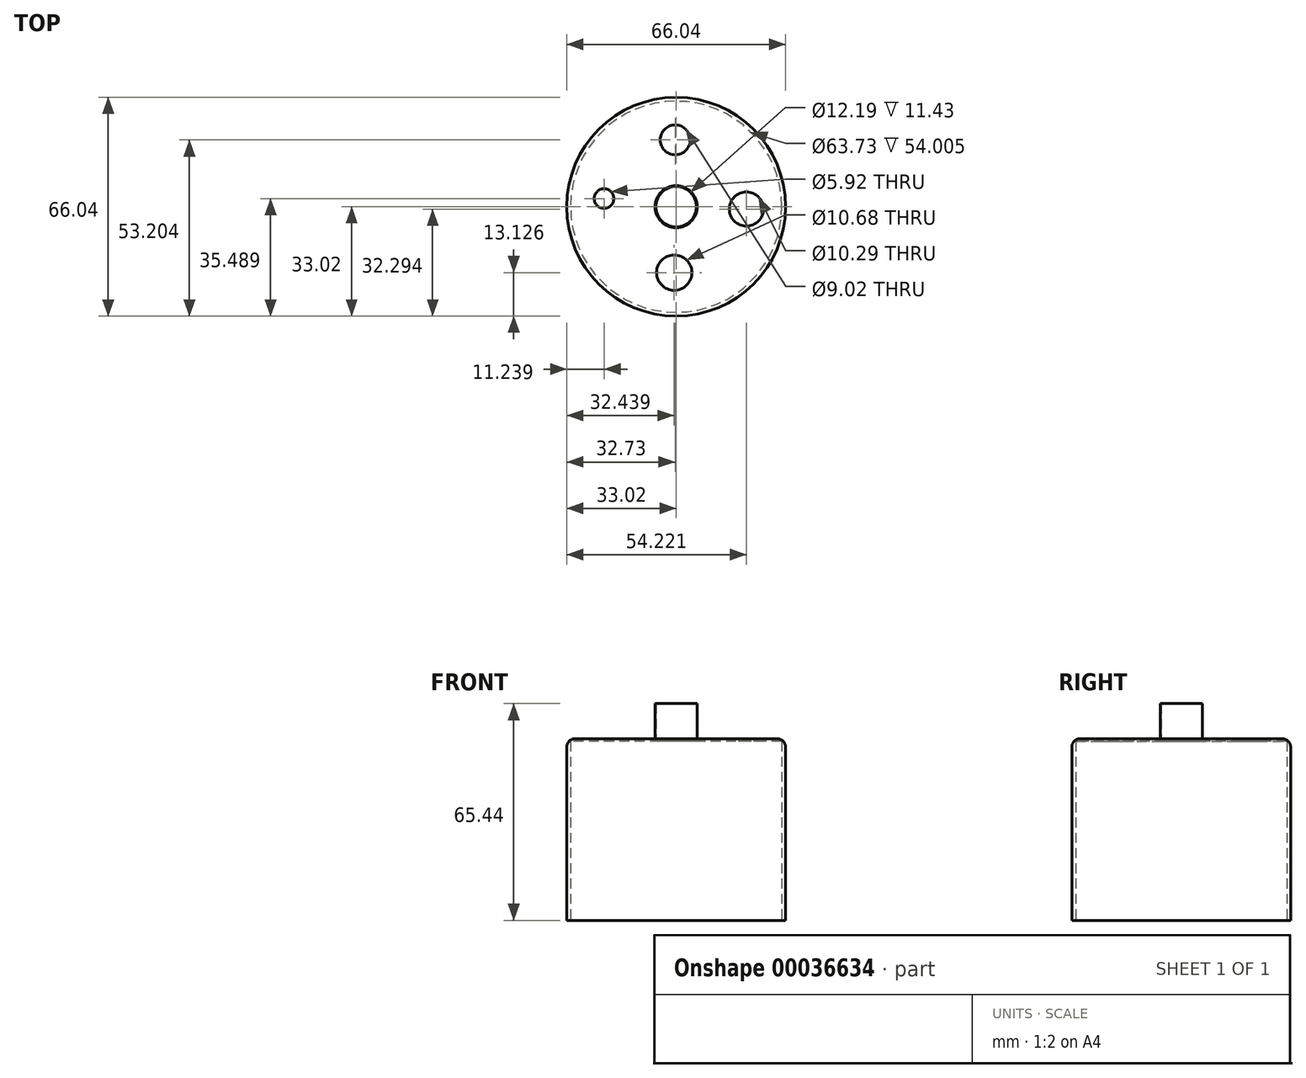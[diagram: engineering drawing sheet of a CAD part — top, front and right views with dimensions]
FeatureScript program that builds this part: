
annotation { "Feature Type Name" : "Feature", "Feature Type Description" : "" }
export const myFeature = defineFeature(function(context is Context, id is Id, definition is map)
    precondition{}
    {
        {
            var Q0;
            Q0=qCreatedBy(makeId("Top.planeOp"),FACE);
            var sketch = newSketch(context, id + "F0", { "sketchPlane" : qUnion([Q0])});
            skCircle(sketch, "E0", {"center": v(0, 0) * mm, "radius": 27.05 * mm});
            skSolve(sketch);
        }
        {
            var Q0;
            Q0=qCreatedBy(makeId("Top.planeOp"),FACE);
            cPlane(context, id + "F1", {"entities" : qUnion([Q0]), "cplaneType" : CPlaneType.OFFSET, "offset" : 10.16 * mm, "width" : 152.4 * mm, "height" : 152.4 * mm});
        }
        {
            var Q0;
            Q0=qCreatedBy(id+"F1.planeOp",FACE);
            var sketch = newSketch(context, id + "F2", { "sketchPlane" : qUnion([Q0])});
            skCircle(sketch, "E1", {"center": v(0, 0) * mm, "radius": 33.02 * mm});
            skSolve(sketch);
        }
        {
            var Q0;
            Q0 = qSketchRegion(id + "F0", true);
            var Q1;
            Q1 = qSketchRegion(id + "F2", true);
            loft(context, id + "F3", {"sheetProfilesArray" : [{ "sheetProfileEntities" : qUnion([Q0]) }, { "sheetProfileEntities" : qUnion([Q1]) }]});
        }
        {
            var Q0;
            Q0=makeQuery(id+"F3.opLoft","CAP_FACE",FACE,{"disambiguationData":[OSD([makeQuery(id+"F2.imprint","IMPRINT",FACE,{"disambiguationData":[TD([[makeQuery(id+"F2.imprint","IMPRINT",EDGE,{"derivedFrom":sQuery(id+"F2.wireOp",EDGE,"E1")}),1.0]])]})])],"isStart":true});
            extrude(context, id + "F4", {"entities" : qUnion([Q0]), "operationType" : NewBodyOperationType.ADD, "depth" : 112.52 * mm});
        }
        {
            var Q0;
            Q0=makeQuery(id+"F3.opLoft","CAP_FACE",FACE,{"disambiguationData":[OSD([makeQuery(id+"F0.imprint","IMPRINT",FACE,{"disambiguationData":[TD([[makeQuery(id+"F0.imprint","IMPRINT",EDGE,{"derivedFrom":sQuery(id+"F0.wireOp",EDGE,"E0")}),1.0]])]})])],"isStart":true});
            cPlane(context, id + "F5", {"entities" : qUnion([Q0]), "cplaneType" : CPlaneType.OFFSET, "offset" : 0.25 * mm, "width" : 152.4 * mm, "height" : 152.4 * mm});
        }
        {
            var Q0;
            Q0=qCreatedBy(id+"F1.planeOp",FACE);
            var sketch = newSketch(context, id + "F6", { "sketchPlane" : qUnion([Q0])});
            skCircle(sketch, "E2", {"center": v(0, 0) * mm, "radius": 31.87 * mm});
            skSolve(sketch);
        }
        {
            var Q0;
            Q0=makeQuery(id+"F3.opLoft","CAP_FACE",FACE,{"disambiguationData":[OSD([makeQuery(id+"F0.imprint","IMPRINT",FACE,{"disambiguationData":[TD([[makeQuery(id+"F0.imprint","IMPRINT",EDGE,{"derivedFrom":sQuery(id+"F0.wireOp",EDGE,"E0")}),1.0]])]})])],"isStart":true});
            var sketch = newSketch(context, id + "F7", { "sketchPlane" : qUnion([Q0])});
            skLineSegment(sketch, "E3", {"start": v(8.97, 14.53) * mm, "end": v(-9, 14.53) * mm});
            skArc(sketch, "E4", {"start": v(8.97, 14.53) * mm, "mid": v(-0.01, 22.72) * mm, "end": v(-9, 14.53) * mm});
            skSolve(sketch);
        }
        {
            var Q0;
            Q0 = qSketchRegion(id + "F7", true);
            extrude(context, id + "F8", {"entities" : qUnion([Q0]), "operationType" : NewBodyOperationType.REMOVE, "oppositeDirection" : true, "depth" : 25.4 * mm});
        }
        {
            var Q0;
            Q0=qCreatedBy(id+"F5.planeOp",FACE);
            cPlane(context, id + "F9", {"entities" : qUnion([Q0]), "cplaneType" : CPlaneType.OFFSET, "offset" : 1.27 * mm, "oppositeDirection" : true, "width" : 152.4 * mm, "height" : 152.4 * mm});
        }
        {
            var Q0;
            Q0=qCreatedBy(id+"F9.planeOp",FACE);
            var sketch = newSketch(context, id + "F10", { "sketchPlane" : qUnion([Q0])});
            skCircle(sketch, "E5", {"center": v(0, 0) * mm, "radius": 27.1 * mm});
            skSolve(sketch);
        }
        {
            var Q1;
            Q1 = qSketchRegion(id + "F6", true);
            var Q2;
            Q2 = qSketchRegion(id + "F10", true);
            loft(context, id + "F11", {"operationType" : NewBodyOperationType.REMOVE, "sheetProfilesArray" : [{ "sheetProfileEntities" : qUnion([Q1]) }, { "sheetProfileEntities" : qUnion([Q2]) }]});
        }
        {
            var Q0;
            Q0 = qSketchRegion(id + "F6", true);
            extrude(context, id + "F12", {"entities" : qUnion([Q0]), "operationType" : NewBodyOperationType.REMOVE, "depth" : 111.68 * mm});
        }
        {
            var Q0;
            Q0=makeQuery(id+"F4.opExtrude","CAP_FACE",FACE,{"disambiguationData":[OSD([makeQuery(id+"F2.imprint","IMPRINT",FACE,{"disambiguationData":[TD([[makeQuery(id+"F2.imprint","IMPRINT",EDGE,{"derivedFrom":sQuery(id+"F2.wireOp",EDGE,"E1")}),1.0]])]})])],"isStart":false});
            var sketch = newSketch(context, id + "F13", { "sketchPlane" : qUnion([Q0])});
            skCircle(sketch, "E6", {"center": v(0, 0) * mm, "radius": 6.1 * mm});
            skCircle(sketch, "E7", {"center": v(0, 0) * mm, "radius": 6.35 * mm});
            skSolve(sketch);
        }
        {
            var Q0;
            Q0 = qSketchRegion(id + "F13", true);
            extrude(context, id + "F14", {"entities" : qUnion([Q0]), "operationType" : NewBodyOperationType.ADD, "depth" : 25.4 * mm});
        }
        {
            var Q0;
            Q0=makeQuery(id+"F14.boolean.opBoolean","SPLIT",FACE,{"disambiguationData":[TD([makeQuery(id+"F14.opExtrude","SWEPT_FACE",FACE,{"disambiguationData":[OSD([sQuery(id+"F13.wireOp",EDGE,"E6")])]})])],"derivedFrom":makeQuery(id+"F4.opExtrude","CAP_FACE",FACE,{"disambiguationData":[OSD([makeQuery(id+"F2.imprint","IMPRINT",FACE,{"disambiguationData":[TD([[makeQuery(id+"F2.imprint","IMPRINT",EDGE,{"derivedFrom":sQuery(id+"F2.wireOp",EDGE,"E1")}),1.0]])]})])],"isStart":false})});
            extrude(context, id + "F15", {"entities" : qUnion([Q0]), "operationType" : NewBodyOperationType.REMOVE, "oppositeDirection" : true, "depth" : 25.4 * mm});
        }
        {
            var Q0;
            Q0=qCreatedBy(makeId("Right.planeOp"),FACE);
            var sketch = newSketch(context, id + "F16", { "sketchPlane" : qUnion([Q0])});
            skLineSegment(sketch, "E8.bottom", {"start": v(51.64, -12.17) * mm, "end": v(-43.74, -12.17) * mm});
            skLineSegment(sketch, "E8.top", {"start": v(51.64, 67.83) * mm, "end": v(-43.74, 67.83) * mm});
            skLineSegment(sketch, "E8.left", {"start": v(51.64, -12.17) * mm, "end": v(51.64, 67.83) * mm});
            skLineSegment(sketch, "E8.right", {"start": v(-43.74, -12.17) * mm, "end": v(-43.74, 67.83) * mm});
            skSolve(sketch);
        }
        {
            var Q0;
            Q0 = qSketchRegion(id + "F16", true);
            extrude(context, id + "F17", {"entities" : qUnion([Q0]), "operationType" : NewBodyOperationType.REMOVE, "oppositeDirection" : true, "depth" : 50.8 * mm, "hasSecondDirection" : true, "secondDirectionOppositeDirection" : false, "secondDirectionDepth" : 50.8 * mm});
        }
        {
            var Q0;
            {var subQ0=sQuery(id+"F2.wireOp",EDGE,"E1");Q0=makeQuery(id+"F14.boolean.opBoolean","SPLIT",FACE,{"disambiguationData":[TD([makeQuery(id+"F14.opExtrude","SWEPT_FACE",FACE,{"disambiguationData":[OSD([sQuery(id+"F13.wireOp",EDGE,"E7")])]})])],"derivedFrom":makeQuery(id+"F4.opExtrude","CAP_FACE",FACE,{"disambiguationData":[OSD([makeQuery(id+"F2.imprint","IMPRINT",FACE,{"disambiguationData":[TD([[makeQuery(id+"F2.imprint","IMPRINT",EDGE,{"derivedFrom":subQ0}),1.0]])]})])],"isStart":false})});}
            var sketch = newSketch(context, id + "F18", { "sketchPlane" : qUnion([Q0])});
            skCircle(sketch, "E9", {"center": v(-0.3, 20.18) * mm, "radius": 4.5 * mm});
            skCircle(sketch, "E10", {"center": v(21.2, -0.73) * mm, "radius": 5.15 * mm});
            skCircle(sketch, "E11", {"center": v(-0.58, -19.9) * mm, "radius": 5.34 * mm});
            skCircle(sketch, "E12", {"center": v(-21.78, 2.47) * mm, "radius": 2.96 * mm});
            skSolve(sketch);
        }
        {
            var Q0;
            Q0 = qSketchRegion(id + "F18", true);
            extrude(context, id + "F19", {"entities" : qUnion([Q0]), "operationType" : NewBodyOperationType.REMOVE, "oppositeDirection" : true, "depth" : 25.4 * mm});
        }
        {
            var Q0;
            Q0=makeQuery(id+"F4.opExtrude","CAP_EDGE",EDGE,{"disambiguationData":[OSD([sQuery(id+"F0.wireOp",EDGE,"E0"),sQuery(id+"F2.wireOp",EDGE,"E1")])],"isStart":false});
            fillet(context, id + "F20", {"entities" : qUnion([Q0]), "radius" : 2.54 * mm, "tangentPropagation" : true, "allowEdgeOverflow" : false});
        }
        {
            var Q0;
            Q0=qCreatedBy(makeId("Front.planeOp"),FACE);
            var sketch = newSketch(context, id + "F21", { "sketchPlane" : qUnion([Q0])});
            skLineSegment(sketch, "E13.bottom", {"start": v(15.14, 133.27) * mm, "end": v(-14.22, 133.27) * mm});
            skLineSegment(sketch, "E13.top", {"start": v(15.14, 149.78) * mm, "end": v(-14.22, 149.78) * mm});
            skLineSegment(sketch, "E13.left", {"start": v(15.14, 133.27) * mm, "end": v(15.14, 149.78) * mm});
            skLineSegment(sketch, "E13.right", {"start": v(-14.22, 133.27) * mm, "end": v(-14.22, 149.78) * mm});
            skSolve(sketch);
        }
        {
            var Q0;
            Q0 = qSketchRegion(id + "F21", true);
            extrude(context, id + "F22", {"entities" : qUnion([Q0]), "operationType" : NewBodyOperationType.REMOVE, "oppositeDirection" : true, "depth" : 25.4 * mm, "hasSecondDirection" : true, "secondDirectionOppositeDirection" : false, "secondDirectionDepth" : 25.4 * mm});
        }
    });
